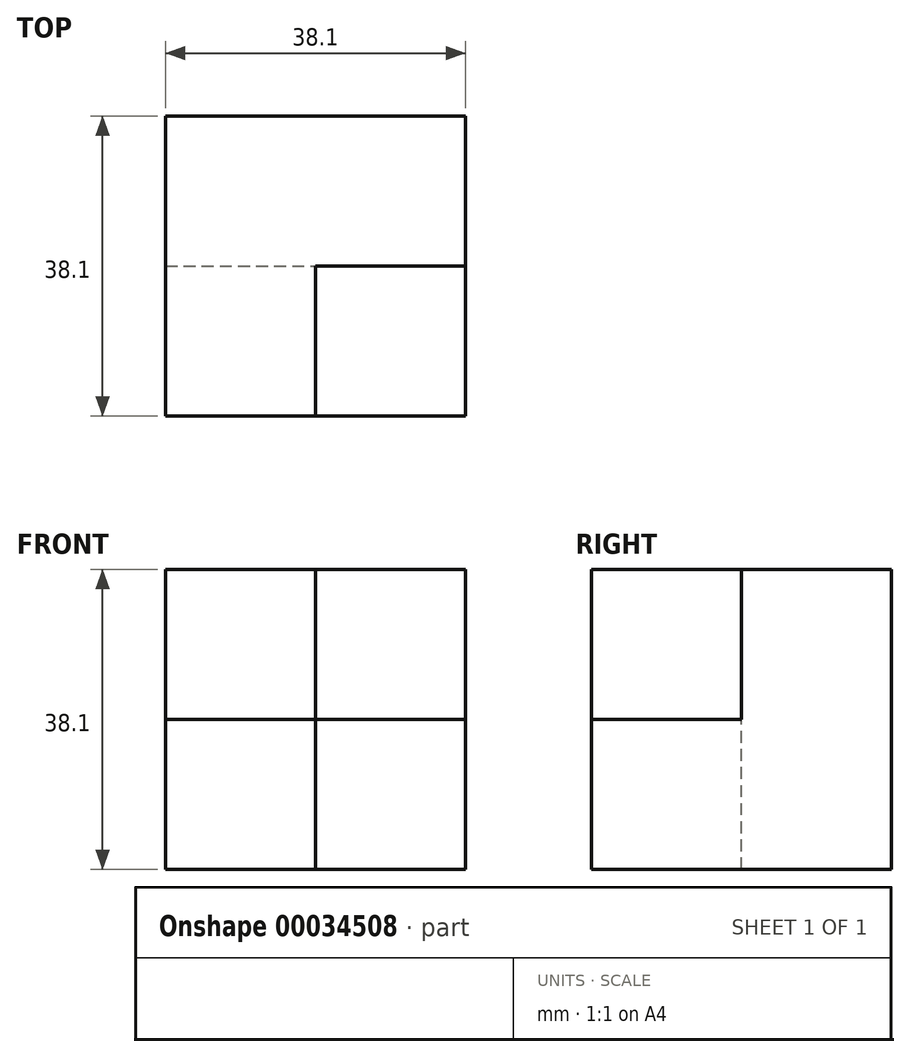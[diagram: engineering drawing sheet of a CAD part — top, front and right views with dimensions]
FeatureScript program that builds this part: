
annotation { "Feature Type Name" : "Feature", "Feature Type Description" : "" }
export const myFeature = defineFeature(function(context is Context, id is Id, definition is map)
    precondition{}
    {
        {
            var Q0;
            Q0=qCreatedBy(makeId("Front.planeOp"),FACE);
            var sketch = newSketch(context, id + "F0", { "sketchPlane" : qUnion([Q0])});
            skLineSegment(sketch, "E0.bottom", {"start": v(0, 0) * mm, "end": v(38.1, 0) * mm});
            skLineSegment(sketch, "E0.top", {"start": v(0, 38.1) * mm, "end": v(38.1, 38.1) * mm});
            skLineSegment(sketch, "E0.left", {"start": v(0, 0) * mm, "end": v(0, 38.1) * mm});
            skLineSegment(sketch, "E0.right", {"start": v(38.1, 0) * mm, "end": v(38.1, 38.1) * mm});
            skSolve(sketch);
        }
        {
            var Q0;
            Q0=makeQuery(id+"F0.imprint","IMPRINT",FACE,{"disambiguationData":[TD([[makeQuery(id+"F0.imprint","IMPRINT",EDGE,{"derivedFrom":sQuery(id+"F0.wireOp",EDGE,"E0.bottom")}),1.0]])]});
            extrude(context, id + "F1", {"entities" : qUnion([Q0]), "depth" : 19.05 * mm});
        }
        {
            var Q0;
            Q0=makeQuery(id+"F1.opExtrude","CAP_FACE",FACE,{"disambiguationData":[OSD([sQuery(id+"F0.wireOp",EDGE,"E0.bottom"),sQuery(id+"F0.wireOp",EDGE,"E0.top"),sQuery(id+"F0.wireOp",EDGE,"E0.left"),sQuery(id+"F0.wireOp",EDGE,"E0.right")])],"isStart":false});
            var sketch = newSketch(context, id + "F2", { "sketchPlane" : qUnion([Q0])});
            skLineSegment(sketch, "E1.bottom", {"start": v(0, 38.1) * mm, "end": v(19.05, 38.1) * mm});
            skLineSegment(sketch, "E1.top", {"start": v(0, 19.05) * mm, "end": v(19.05, 19.05) * mm});
            skLineSegment(sketch, "E1.left", {"start": v(0, 38.1) * mm, "end": v(0, 19.05) * mm});
            skLineSegment(sketch, "E1.right", {"start": v(19.05, 38.1) * mm, "end": v(19.05, 19.05) * mm});
            skSolve(sketch);
        }
        {
            var Q0;
            Q0 = qSketchRegion(id + "F2", true);
            extrude(context, id + "F3", {"entities" : qUnion([Q0]), "operationType" : NewBodyOperationType.ADD, "depth" : 19.05 * mm});
        }
        {
            var Q0;
            Q0=makeQuery(id+"F1.opExtrude","CAP_FACE",FACE,{"disambiguationData":[OSD([sQuery(id+"F0.wireOp",EDGE,"E0.bottom"),sQuery(id+"F0.wireOp",EDGE,"E0.top"),sQuery(id+"F0.wireOp",EDGE,"E0.left"),sQuery(id+"F0.wireOp",EDGE,"E0.right")])],"isStart":false});
            var sketch = newSketch(context, id + "F4", { "sketchPlane" : qUnion([Q0])});
            skLineSegment(sketch, "E2.bottom", {"start": v(38.1, 0) * mm, "end": v(19.05, 0) * mm});
            skLineSegment(sketch, "E2.top", {"start": v(38.1, 19.05) * mm, "end": v(19.05, 19.05) * mm});
            skLineSegment(sketch, "E2.left", {"start": v(38.1, 0) * mm, "end": v(38.1, 19.05) * mm});
            skLineSegment(sketch, "E2.right", {"start": v(19.05, 0) * mm, "end": v(19.05, 19.05) * mm});
            skSolve(sketch);
        }
        {
            var Q0;
            Q0=makeQuery(id+"F3.opExtrude","SWEPT_EDGE",EDGE,{"disambiguationData":[OSD([sQuery(id+"F2.wireOp",EDGE,"E1.top"),sQuery(id+"F2.wireOp",EDGE,"E1.right")])]});
            chamfer(context, id + "F5", {"entities" : qUnion([Q0]), "width" : 0.03 * mm, "tangentPropagation" : true});
        }
        {
            var Q0;
            Q0 = qSketchRegion(id + "F4", true);
            extrude(context, id + "F6", {"entities" : qUnion([Q0]), "operationType" : NewBodyOperationType.ADD, "depth" : 19.05 * mm});
        }
    });
